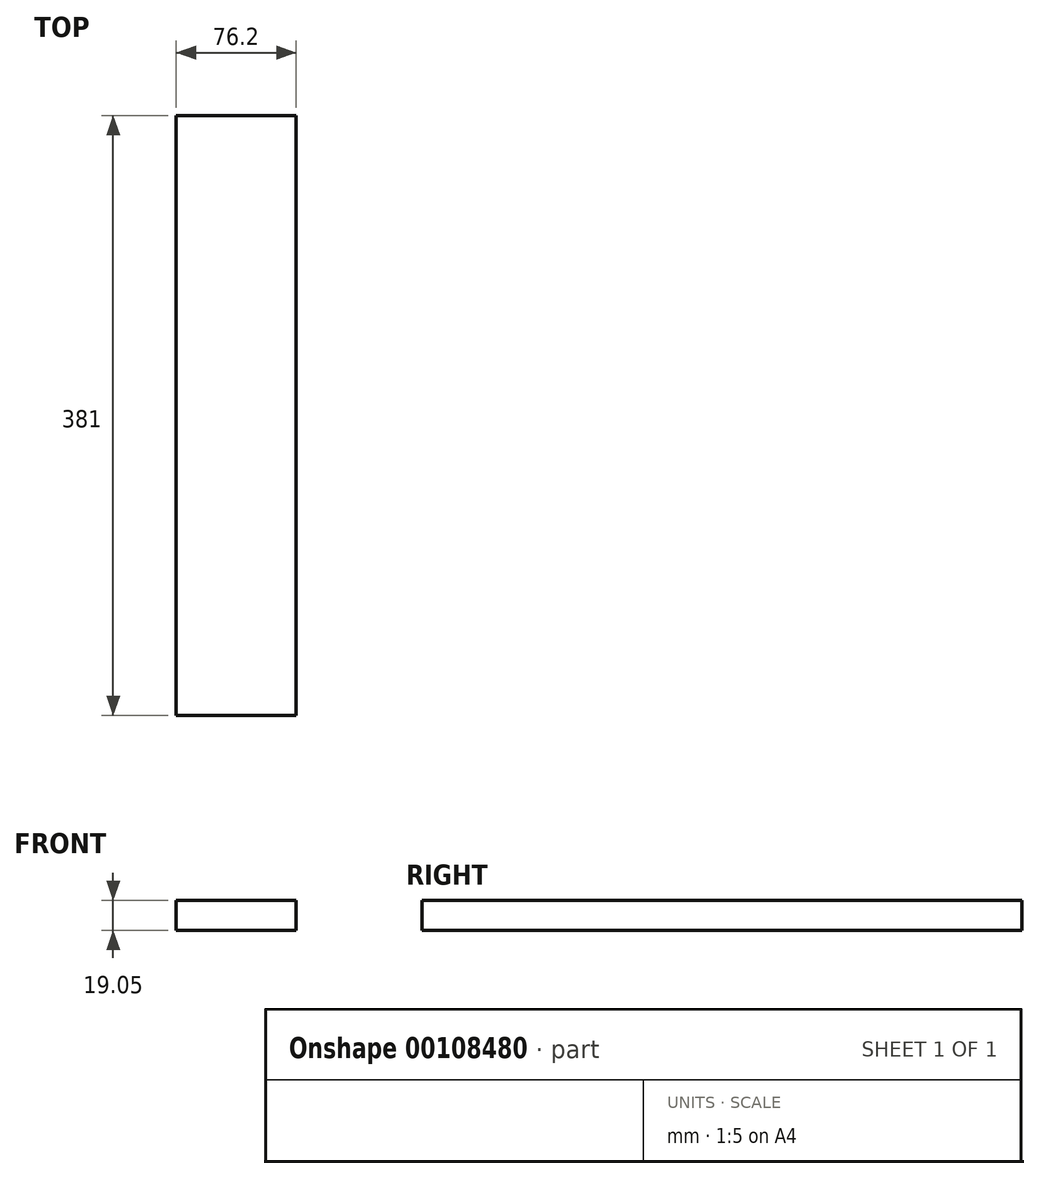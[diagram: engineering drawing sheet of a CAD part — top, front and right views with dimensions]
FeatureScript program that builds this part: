
annotation { "Feature Type Name" : "Feature", "Feature Type Description" : "" }
export const myFeature = defineFeature(function(context is Context, id is Id, definition is map)
    precondition{}
    {
        {
            var Q0;
            Q0=qCreatedBy(makeId("Front.planeOp"),FACE);
            var sketch = newSketch(context, id + "F0", { "sketchPlane" : qUnion([Q0])});
            skLineSegment(sketch, "E0.bottom", {"start": v(0, 0) * mm, "end": v(76.2, 0) * mm});
            skLineSegment(sketch, "E0.top", {"start": v(0, 19.05) * mm, "end": v(76.2, 19.05) * mm});
            skLineSegment(sketch, "E0.left", {"start": v(0, 0) * mm, "end": v(0, 19.05) * mm});
            skLineSegment(sketch, "E0.right", {"start": v(76.2, 0) * mm, "end": v(76.2, 19.05) * mm});
            skSolve(sketch);
        }
        {
            var Q0;
            Q0 = qSketchRegion(id + "F0", true);
            extrude(context, id + "F1", {"entities" : qUnion([Q0]), "depth" : 381 * mm});
        }
    });
